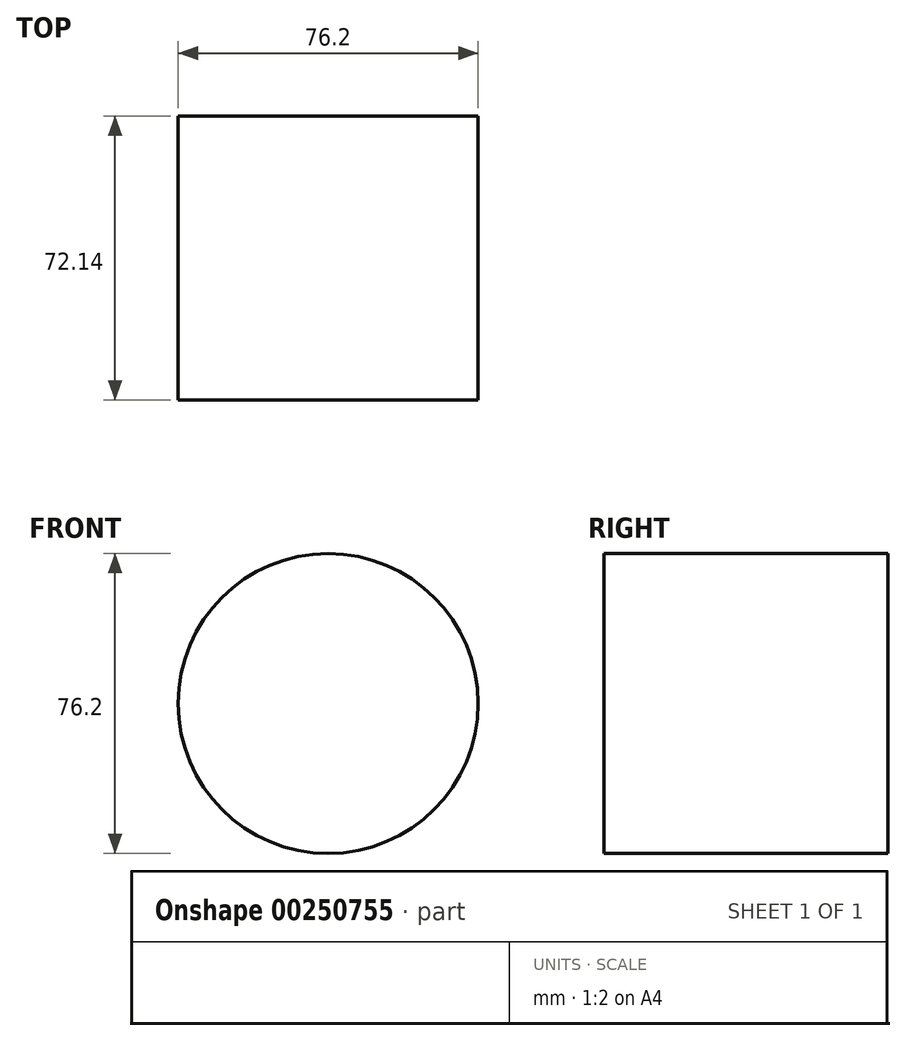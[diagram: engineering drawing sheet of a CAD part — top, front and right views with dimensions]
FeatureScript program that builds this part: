
annotation { "Feature Type Name" : "Feature", "Feature Type Description" : "" }
export const myFeature = defineFeature(function(context is Context, id is Id, definition is map)
    precondition{}
    {
        {
            var Q0;
            Q0=qCreatedBy(makeId("Front.planeOp"),FACE);
            var sketch = newSketch(context, id + "F0", { "sketchPlane" : qUnion([Q0])});
            skCircle(sketch, "E0", {"center": v(0, 0) * mm, "radius": 38.1 * mm});
            skSolve(sketch);
        }
        {
            var Q0;
            Q0=makeQuery(id+"F0.imprint","IMPRINT",FACE,{"disambiguationData":[TD([[makeQuery(id+"F0.imprint","IMPRINT",EDGE,{"derivedFrom":sQuery(id+"F0.wireOp",EDGE,"E0")}),1.0]])]});
            extrude(context, id + "F1", {"entities" : qUnion([Q0]), "depth" : 72.14 * mm});
        }
    });
